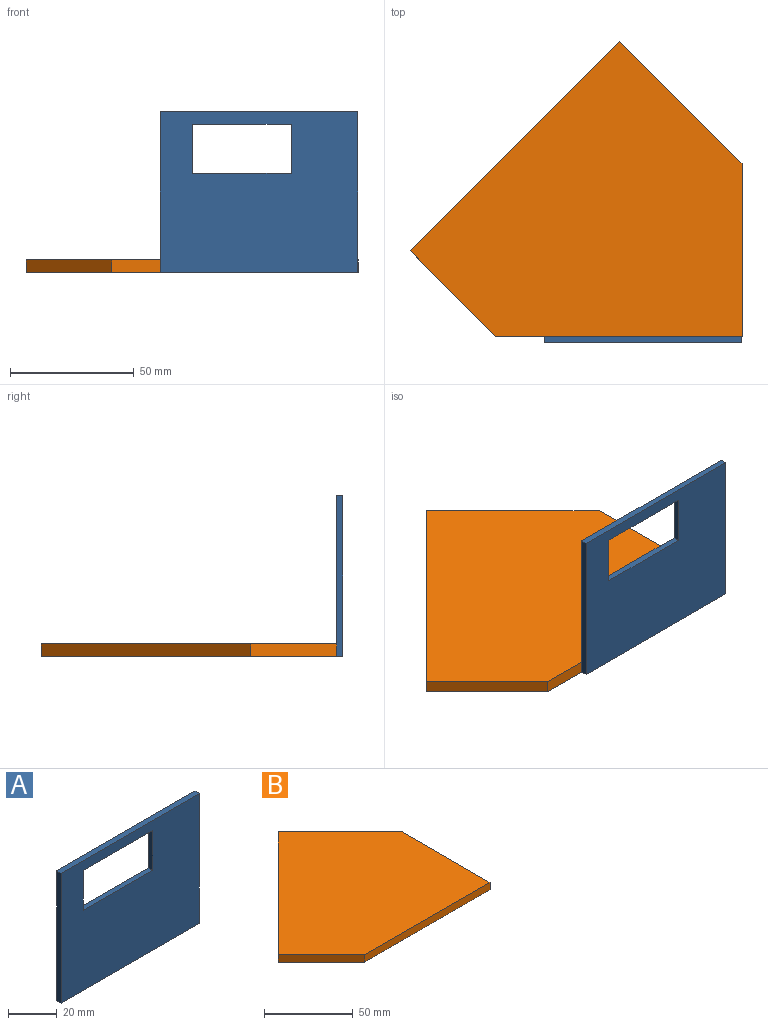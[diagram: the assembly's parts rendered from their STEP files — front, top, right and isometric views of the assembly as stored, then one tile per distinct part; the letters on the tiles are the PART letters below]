
ASSEMBLY  parts=2 mates=1
PART A: 20 faces, bbox 80x2.5x65 mm
  f0: plane 42x22mm, normal (0,1,0), area 124mm2, adj f5,f6,f7,f8,f14,f15,f16,f17
  f1: plane 80x65mm, normal (0,1,0), area 286mm2, adj f2,f3,f4,f9,f11,f12,f13,f18
  f2: plane 80x2.5mm, normal (0,0,-1), area 200mm2, adj f1,f3,f9,f10
  f3: plane 65x2.5mm, normal (1,0,0), area 162.5mm2, adj f1,f2,f4,f10
  f4: plane 80x2.5mm, normal (0,0,1), area 200mm2, adj f1,f3,f9,f10
  f5: plane 20x2.5mm, normal (1,0,0), area 50mm2, adj f0,f6,f8,f10
  f6: plane 40x2.5mm, normal (0,0,-1), area 100mm2, adj f0,f5,f7,f10
  f7: plane 20x2.5mm, normal (-1,0,0), area 50mm2, adj f0,f6,f8,f10
  f8: plane 40x2.5mm, normal (0,0,1), area 100mm2, adj f0,f5,f7,f10
  f9: plane 65x2.5mm, normal (-1,0,0), area 162.5mm2, adj f1,f2,f4,f10
  f10: plane 80x65mm, normal (0,-1,0), area 4400mm2, adj f2,f3,f4,f5,f6,f7,f8,f9
  f11: plane 78x1.5mm, normal (0,0,1), area 117mm2, adj f1,f12,f18,f19
  f12: plane 63x1.5mm, normal (-1,0,0), area 94.5mm2, adj f1,f11,f13,f19
  f13: plane 78x1.5mm, normal (0,0,-1), area 117mm2, adj f1,f12,f18,f19
  f14: plane 22x1.5mm, normal (-1,0,0), area 33mm2, adj f0,f15,f17,f19
  f15: plane 42x1.5mm, normal (0,0,1), area 63mm2, adj f0,f14,f16,f19
  f16: plane 22x1.5mm, normal (1,0,0), area 33mm2, adj f0,f15,f17,f19
  f17: plane 42x1.5mm, normal (0,0,-1), area 63mm2, adj f0,f14,f16,f19
  f18: plane 63x1.5mm, normal (1,0,0), area 94.5mm2, adj f1,f11,f13,f19
  f19: plane 78x63mm, normal (0,1,0), area 3990mm2, adj f11,f12,f13,f14,f15,f16,f17,f18
PART B: 13 faces, bbox 134.4x119.5x5 mm
  f0: plane 134.35x119.5mm, normal (0,0,-1), area 997.8mm2, adj f1,f2,f3,f4,f5,f7,f8,f9
  f1: plane 99.71x5mm, normal (0,-1,0), area 498.5mm2, adj f0,f2,f5,f6
  f2: plane 70x5mm, normal (1,0,0), area 350mm2, adj f0,f1,f3,f6
  f3: plane 49.5x49.5mm, normal (0.71,0.71,0), area 350mm2, adj f0,f2,f4,f6
  f4: plane 84.85x84.85mm, normal (-0.71,0.71,0), area 600mm2, adj f0,f3,f5,f6
  f5: plane 34.64x34.64mm, normal (-0.71,-0.71,0), area 245mm2, adj f0,f1,f4,f6
  f6: plane 134.35x119.5mm, normal (0,0,1), area 10629.4mm2, adj f1,f2,f3,f4,f5
  f7: plane 96.17x2.5mm, normal (0,1,0), area 240.4mm2, adj f0,f8,f11,f12
  f8: plane 66.46x2.5mm, normal (-1,0,0), area 166.2mm2, adj f0,f7,f9,f12
  f9: plane 47x47mm, normal (-0.71,-0.71,0), area 166.2mm2, adj f0,f8,f10,f12
  f10: plane 81.32x81.32mm, normal (0.71,-0.71,0), area 287.5mm2, adj f0,f9,f11,f12
  f11: plane 32.14x32.14mm, normal (0.71,0.71,0), area 113.6mm2, adj f0,f7,f10,f12
  f12: plane 128.31x113.46mm, normal (0,0,-1), area 9631.6mm2, adj f7,f8,f9,f10,f11
PLACE A t=(56.41,-48.2,3.22)mm
PLACE B t=(6.91,-13.56,8.22)mm
MATE fastened A.f1 <-> B.f1  axis (0,1,0) through (56.41,-48.2,3.22)mm
